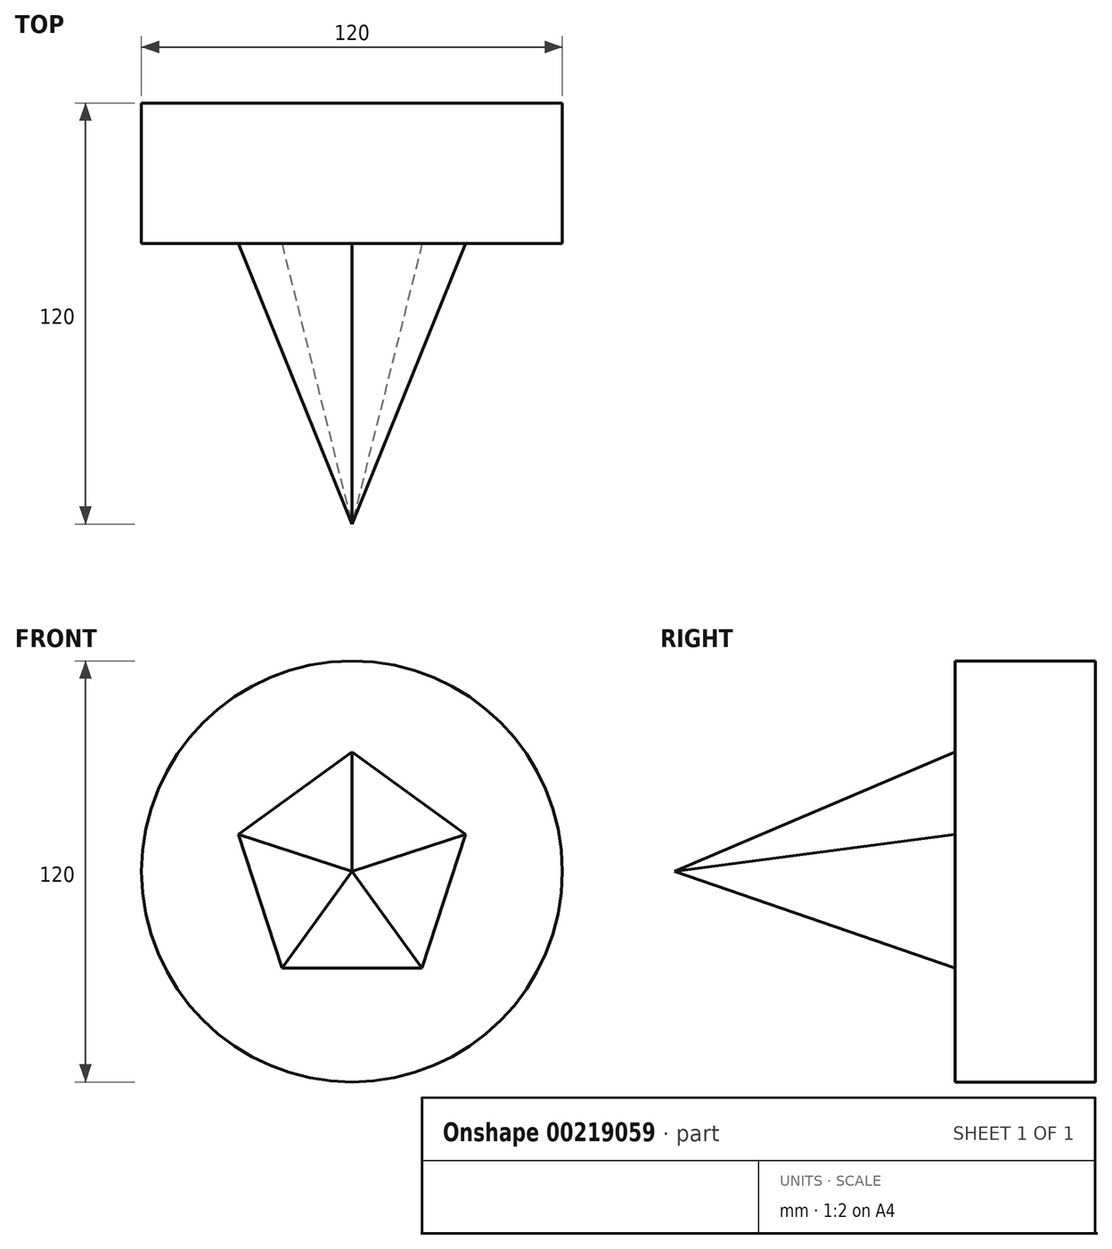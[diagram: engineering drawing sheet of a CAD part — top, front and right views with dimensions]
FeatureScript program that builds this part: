
annotation { "Feature Type Name" : "Feature", "Feature Type Description" : "" }
export const myFeature = defineFeature(function(context is Context, id is Id, definition is map)
    precondition{}
    {
        {
            var Q0;
            Q0=qCreatedBy(makeId("Front.planeOp"),FACE);
            var sketch = newSketch(context, id + "F0", { "sketchPlane" : qUnion([Q0])});
            skCircle(sketch, "E0", {"center": v(0, 0) * mm, "radius": 60 * mm});
            skSolve(sketch);
        }
        {
            var Q0;
            Q0 = qSketchRegion(id + "F0", true);
            extrude(context, id + "F1", {"entities" : qUnion([Q0]), "depth" : 40 * mm});
        }
        {
            var Q0;
            Q0=makeQuery(id+"F1.opExtrude","CAP_FACE",FACE,{"disambiguationData":[OSD([sQuery(id+"F0.wireOp",EDGE,"E0")])],"isStart":false});
            var sketch = newSketch(context, id + "F2", { "sketchPlane" : qUnion([Q0])});
            skCircle(sketch, "E1.cCircle", {"center": v(0, 0) * mm, "radius": 27.53 * mm, "construction": true});
            skLineSegment(sketch, "E1.0", {"start": v(0, 34.03) * mm, "end": v(32.36, 10.51) * mm});
            skLineSegment(sketch, "E1.1", {"start": v(32.36, 10.51) * mm, "end": v(20, -27.53) * mm});
            skLineSegment(sketch, "E1.2", {"start": v(20, -27.53) * mm, "end": v(-20, -27.53) * mm});
            skLineSegment(sketch, "E1.3", {"start": v(-20, -27.53) * mm, "end": v(-32.36, 10.51) * mm});
            skLineSegment(sketch, "E1.4", {"start": v(-32.36, 10.51) * mm, "end": v(0, 34.03) * mm});
            skPoint(sketch, "E1.0.midPoint", {"position": v(16.18, 22.27) * mm});
            skSolve(sketch);
        }
        {
            var Q0;
            Q0=makeQuery(id+"F2.imprint","IMPRINT",FACE,{"disambiguationData":[TD([[makeQuery(id+"F2.imprint","IMPRINT",EDGE,{"derivedFrom":sQuery(id+"F2.wireOp",EDGE,"E1.0")}),1.0]])]});
            cPlane(context, id + "F3", {"entities" : qUnion([Q0]), "cplaneType" : CPlaneType.OFFSET, "offset" : 80 * mm, "width" : 150 * mm, "height" : 150 * mm});
        }
        {
            var Q0;
            Q0=qCreatedBy(id+"F3.planeOp",FACE);
            var sketch = newSketch(context, id + "F4", { "sketchPlane" : qUnion([Q0])});
            skPoint(sketch, "E2", {"position": v(0, 0) * mm});
            skSolve(sketch);
        }
        {
            var Q1;
            Q1=makeQuery(id+"F2.imprint","IMPRINT",FACE,{"disambiguationData":[TD([[makeQuery(id+"F2.imprint","IMPRINT",EDGE,{"derivedFrom":sQuery(id+"F2.wireOp",EDGE,"E1.0")}),-1.0]])]});
            var Q2;
            Q2=sQuery(id+"F4.wireOp",VERTEX,"E2");
            loft(context, id + "F5", {"operationType" : NewBodyOperationType.ADD, "sheetProfilesArray" : [{ "sheetProfileEntities" : qUnion([Q1]) }, { "sheetProfileEntities" : qUnion([Q2]) }]});
        }
    });
